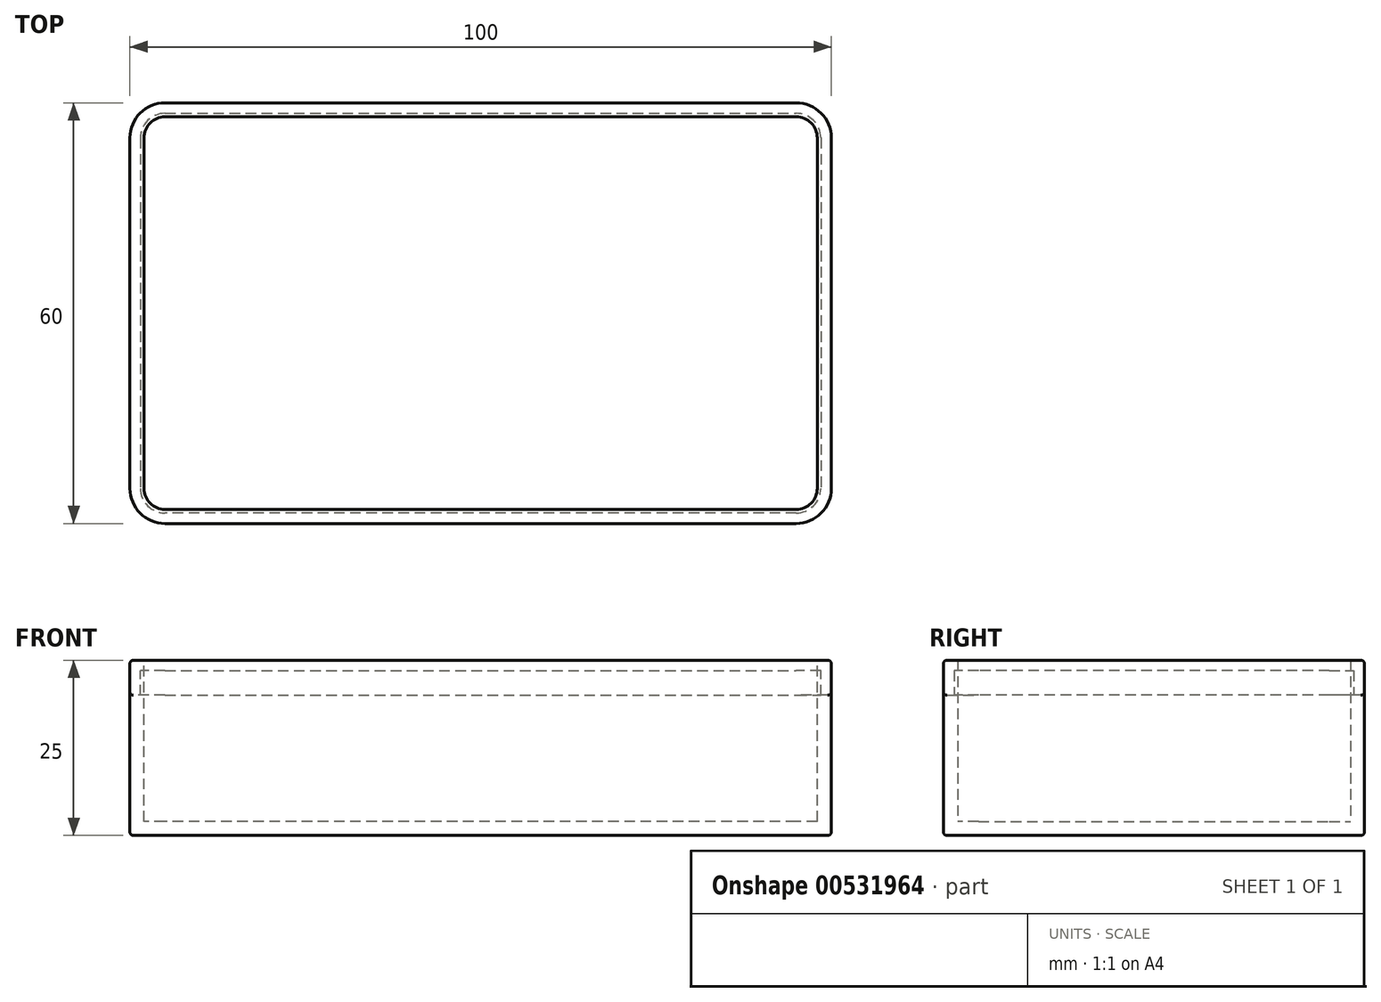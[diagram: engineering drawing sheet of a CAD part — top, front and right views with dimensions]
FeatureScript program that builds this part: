
annotation { "Feature Type Name" : "Feature", "Feature Type Description" : "" }
export const myFeature = defineFeature(function(context is Context, id is Id, definition is map)
    precondition{}
    {
        {
            var Q0;
            Q0=qCreatedBy(makeId("Top.planeOp"),FACE);
            var sketch = newSketch(context, id + "F0", { "sketchPlane" : qUnion([Q0])});
            skLineSegment(sketch, "E0.bottom", {"start": v(45, -30) * mm, "end": v(-45, -30) * mm});
            skLineSegment(sketch, "E0.top", {"start": v(45, 30) * mm, "end": v(-45, 30) * mm});
            skLineSegment(sketch, "E0.left", {"start": v(50, -25) * mm, "end": v(50, 25) * mm});
            skLineSegment(sketch, "E0.right", {"start": v(-50, -25) * mm, "end": v(-50, 25) * mm});
            skPoint(sketch, "E0.middle", {"position": v(0, 0) * mm});
            skPoint(sketch, "E1.visualSharp", {"position": v(-50, 30) * mm});
            skArc(sketch, "E1.filletArc", {"start": v(-45, 30) * mm, "mid": v(-48.54, 28.54) * mm, "end": v(-50, 25) * mm});
            skPoint(sketch, "E2.visualSharp", {"position": v(50, 30) * mm});
            skArc(sketch, "E2.filletArc", {"start": v(50, 25) * mm, "mid": v(48.54, 28.54) * mm, "end": v(45, 30) * mm});
            skPoint(sketch, "E3.visualSharp", {"position": v(50, -30) * mm});
            skArc(sketch, "E3.filletArc", {"start": v(45, -30) * mm, "mid": v(48.54, -28.54) * mm, "end": v(50, -25) * mm});
            skPoint(sketch, "E4.visualSharp", {"position": v(-50, -30) * mm});
            skArc(sketch, "E4.filletArc", {"start": v(-50, -25) * mm, "mid": v(-48.54, -28.54) * mm, "end": v(-45, -30) * mm});
            skSolve(sketch);
        }
        {
            var Q0;
            Q0=qSketchRegion(id+"F0",true);
            extrude(context, id + "F1", {"entities" : qUnion([Q0]), "depth" : 25 * mm, "offsetDistance" : 25 * mm});
        }
        {
            var Q0;
            Q0=makeQuery(id+"F1.opExtrude","CAP_FACE",FACE,{"disambiguationData":[OSD([sQuery(id+"F0.wireOp",EDGE,"E0.bottom"),sQuery(id+"F0.wireOp",EDGE,"E0.top"),sQuery(id+"F0.wireOp",EDGE,"E0.left"),sQuery(id+"F0.wireOp",EDGE,"E0.right"),sQuery(id+"F0.wireOp",EDGE,"E1.filletArc"),sQuery(id+"F0.wireOp",EDGE,"E2.filletArc"),sQuery(id+"F0.wireOp",EDGE,"E3.filletArc"),sQuery(id+"F0.wireOp",EDGE,"E4.filletArc")])],"isStart":false});
            shell(context, id + "F2", {"entities" : qUnion([Q0]), "thickness" : 2 * mm});
        }
        {
            var Q0;
            Q0=makeQuery(id+"F1.opExtrude","CAP_FACE",FACE,{"disambiguationData":[OSD([sQuery(id+"F0.wireOp",EDGE,"E0.bottom"),sQuery(id+"F0.wireOp",EDGE,"E0.top"),sQuery(id+"F0.wireOp",EDGE,"E0.left"),sQuery(id+"F0.wireOp",EDGE,"E0.right"),sQuery(id+"F0.wireOp",EDGE,"E1.filletArc"),sQuery(id+"F0.wireOp",EDGE,"E2.filletArc"),sQuery(id+"F0.wireOp",EDGE,"E3.filletArc"),sQuery(id+"F0.wireOp",EDGE,"E4.filletArc")])],"isStart":false});
            cPlane(context, id + "F3", {"entities" : qUnion([Q0]), "cplaneType" : CPlaneType.OFFSET, "offset" : 5 * mm, "oppositeDirection" : true, "width" : 150 * mm, "height" : 150 * mm});
        }
        {
            var Q0;
            Q0=qCreatedBy(id+"F3.planeOp",FACE);
            var sketch = newSketch(context, id + "F4", { "sketchPlane" : qUnion([Q0])});
            skLineSegment(sketch, "E5.bottom", {"start": v(45, -30) * mm, "end": v(-45, -30) * mm});
            skLineSegment(sketch, "E5.top", {"start": v(45, 30) * mm, "end": v(-45, 30) * mm});
            skLineSegment(sketch, "E5.left", {"start": v(50, -25) * mm, "end": v(50, 25) * mm});
            skLineSegment(sketch, "E5.right", {"start": v(-50, -25) * mm, "end": v(-50, 25) * mm});
            skPoint(sketch, "E5.middle", {"position": v(0, 0) * mm});
            skPoint(sketch, "E6.visualSharp", {"position": v(-50, 30) * mm});
            skArc(sketch, "E6.filletArc", {"start": v(-45, 30) * mm, "mid": v(-48.54, 28.54) * mm, "end": v(-50, 25) * mm});
            skPoint(sketch, "E7.visualSharp", {"position": v(50, 30) * mm});
            skArc(sketch, "E7.filletArc", {"start": v(50, 25) * mm, "mid": v(48.54, 28.54) * mm, "end": v(45, 30) * mm});
            skPoint(sketch, "E8.visualSharp", {"position": v(50, -30) * mm});
            skArc(sketch, "E8.filletArc", {"start": v(45, -30) * mm, "mid": v(48.54, -28.54) * mm, "end": v(50, -25) * mm});
            skPoint(sketch, "E9.visualSharp", {"position": v(-50, -30) * mm});
            skArc(sketch, "E9.filletArc", {"start": v(-50, -25) * mm, "mid": v(-48.54, -28.54) * mm, "end": v(-45, -30) * mm});
            skSolve(sketch);
        }
        {
            var Q0;
            Q0=qSketchRegion(id+"F4",true);
            extrude(context, id + "F5", {"entities" : qUnion([Q0]), "depth" : 5 * mm, "offsetDistance" : 25 * mm});
        }
        {
            var Q0;
            Q0=makeQuery(id+"F5.opExtrude","CAP_EDGE",EDGE,{"disambiguationData":[OSD([sQuery(id+"F4.wireOp",EDGE,"E6.filletArc")])],"isStart":false});
            var Q1;
            Q1=makeQuery(id+"F1.opExtrude","CAP_EDGE",EDGE,{"disambiguationData":[OSD([sQuery(id+"F0.wireOp",EDGE,"E1.filletArc")])],"isStart":true});
            var Q2;
            Q2=makeQuery(id+"F5.opExtrude","CAP_EDGE",EDGE,{"disambiguationData":[OSD([sQuery(id+"F4.wireOp",EDGE,"E6.filletArc")])],"isStart":true});
            var Q3;
            Q3=makeQuery(id+"F1.opExtrude","CAP_EDGE",EDGE,{"disambiguationData":[OSD([sQuery(id+"F0.wireOp",EDGE,"E0.right")])],"isStart":false});
            fillet(context, id + "F6", {"entities" : qUnion([Q0, Q1, Q2, Q3]), "radius" : 0.5 * mm, "tangentPropagation" : true, "allowEdgeOverflow" : false});
        }
        {
            var Q0;
            Q0=makeQuery(id+"F5.opExtrude","CAP_FACE",FACE,{"disambiguationData":[OSD([sQuery(id+"F4.wireOp",EDGE,"E5.bottom"),sQuery(id+"F4.wireOp",EDGE,"E5.top"),sQuery(id+"F4.wireOp",EDGE,"E5.left"),sQuery(id+"F4.wireOp",EDGE,"E5.right"),sQuery(id+"F4.wireOp",EDGE,"E6.filletArc"),sQuery(id+"F4.wireOp",EDGE,"E7.filletArc"),sQuery(id+"F4.wireOp",EDGE,"E8.filletArc"),sQuery(id+"F4.wireOp",EDGE,"E9.filletArc")])],"isStart":true});
            shell(context, id + "F7", {"entities" : qUnion([Q0]), "thickness" : 1.5 * mm});
        }
    });
